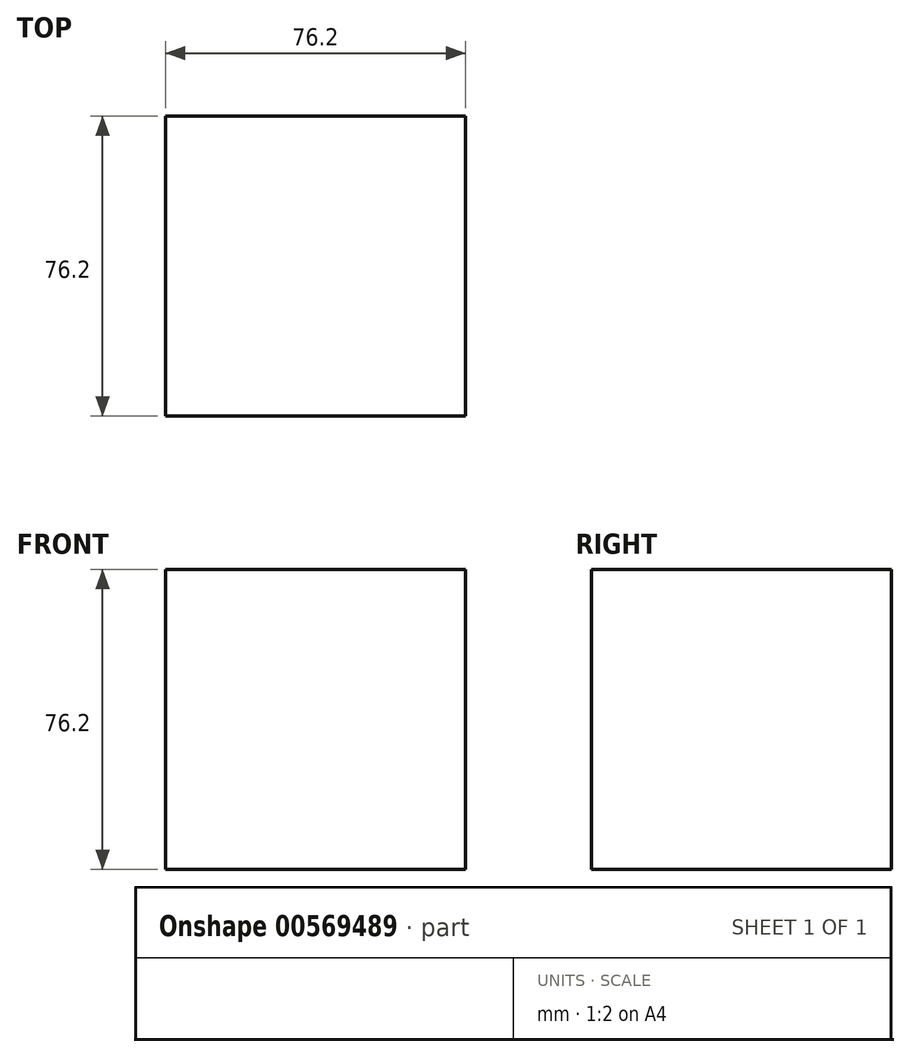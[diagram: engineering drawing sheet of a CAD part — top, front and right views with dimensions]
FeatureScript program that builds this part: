
annotation { "Feature Type Name" : "Feature", "Feature Type Description" : "" }
export const myFeature = defineFeature(function(context is Context, id is Id, definition is map)
    precondition{}
    {
        {
            var Q0;
            Q0=qCreatedBy(makeId("Front.planeOp"),FACE);
            var sketch = newSketch(context, id + "F0", { "sketchPlane" : qUnion([Q0])});
            skLineSegment(sketch, "E0.bottom", {"start": v(-93.5, 76.2) * mm, "end": v(-17.3, 76.2) * mm});
            skLineSegment(sketch, "E0.top", {"start": v(-93.5, 0) * mm, "end": v(-17.3, 0) * mm});
            skLineSegment(sketch, "E0.left", {"start": v(-93.5, 76.2) * mm, "end": v(-93.5, 0) * mm});
            skLineSegment(sketch, "E0.right", {"start": v(-17.3, 76.2) * mm, "end": v(-17.3, 0) * mm});
            skSolve(sketch);
        }
        {
            var Q0;
            Q0=makeQuery(id+"F0.imprint","IMPRINT",FACE,{"disambiguationData":[TD([[makeQuery(id+"F0.imprint","IMPRINT",EDGE,{"derivedFrom":sQuery(id+"F0.wireOp",EDGE,"E0.bottom")}),-1.0]])]});
            extrude(context, id + "F1", {"entities" : qUnion([Q0]), "depth" : 76.2 * mm, "offsetDistance" : 25.4 * mm});
        }
    });
